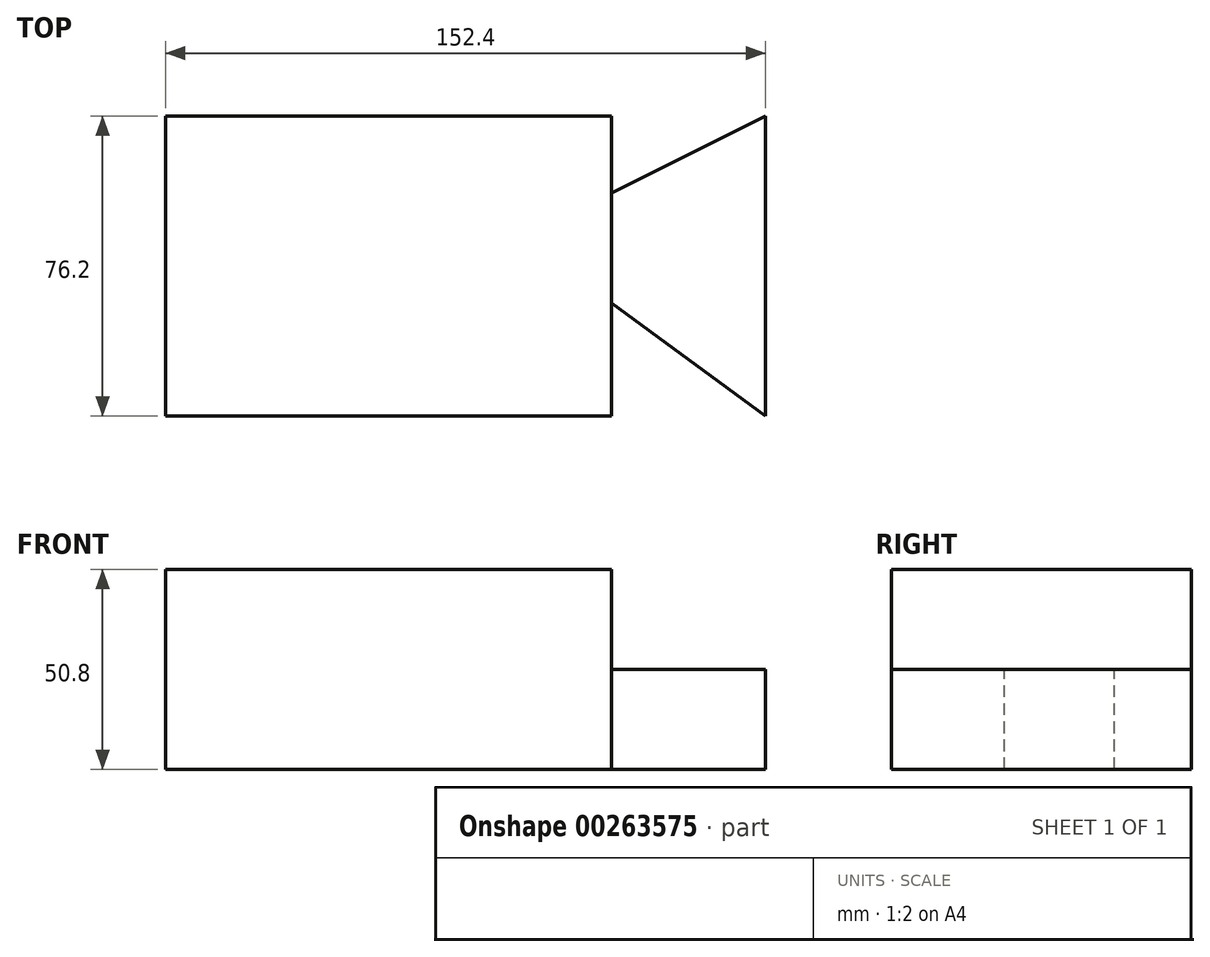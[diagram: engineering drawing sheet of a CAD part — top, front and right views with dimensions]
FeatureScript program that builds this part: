
annotation { "Feature Type Name" : "Feature", "Feature Type Description" : "" }
export const myFeature = defineFeature(function(context is Context, id is Id, definition is map)
    precondition{}
    {
        {
            var Q0;
            Q0=qCreatedBy(makeId("Front.planeOp"),FACE);
            var sketch = newSketch(context, id + "F0", { "sketchPlane" : qUnion([Q0])});
            skLineSegment(sketch, "E0.bottom", {"start": v(-73.83, 13.67) * mm, "end": v(78.57, 13.67) * mm});
            skLineSegment(sketch, "E0.top", {"start": v(-73.83, -37.13) * mm, "end": v(78.57, -37.13) * mm});
            skLineSegment(sketch, "E0.left", {"start": v(-73.83, 13.67) * mm, "end": v(-73.83, -37.13) * mm});
            skLineSegment(sketch, "E0.right", {"start": v(78.57, 13.67) * mm, "end": v(78.57, -37.13) * mm});
            skSolve(sketch);
        }
        {
            var Q0;
            Q0 = qSketchRegion(id + "F0", true);
            extrude(context, id + "F1", {"entities" : qUnion([Q0]), "depth" : 76.2 * mm});
        }
        {
            var Q0;
            Q0=makeQuery(id+"F1.opExtrude","SWEPT_FACE",FACE,{"disambiguationData":[OSD([sQuery(id+"F0.wireOp",EDGE,"E0.bottom")])]});
            var sketch = newSketch(context, id + "F2", { "sketchPlane" : qUnion([Q0])});
            skLineSegment(sketch, "E1", {"start": v(78.57, -76.2) * mm, "end": v(39.48, -47.56) * mm});
            skLineSegment(sketch, "E2", {"start": v(39.48, -19.5) * mm, "end": v(78.57, 0) * mm});
            skLineSegment(sketch, "E3", {"start": v(39.48, -19.5) * mm, "end": v(39.48, 0) * mm});
            skLineSegment(sketch, "E4", {"start": v(39.48, 0) * mm, "end": v(78.57, 0) * mm});
            skLineSegment(sketch, "E5", {"start": v(39.48, -47.56) * mm, "end": v(39.48, -76.2) * mm});
            skLineSegment(sketch, "E6", {"start": v(39.48, -76.2) * mm, "end": v(78.57, -76.2) * mm});
            skSolve(sketch);
        }
        {
            var Q0;
            Q0 = qSketchRegion(id + "F2", true);
            extrude(context, id + "F3", {"entities" : qUnion([Q0]), "operationType" : NewBodyOperationType.REMOVE, "endBound" : BoundingType.THROUGH_ALL, "oppositeDirection" : true, "depth" : 25.4 * mm});
        }
        {
            var Q0;
            Q0=makeQuery(id+"F3.boolean.opBoolean","COPY",FACE,{"derivedFrom":makeQuery(id+"F3.opExtrude","SWEPT_FACE",FACE,{"disambiguationData":[OSD([sQuery(id+"F2.wireOp",EDGE,"E1")])]})});
            var sketch = newSketch(context, id + "F4", { "sketchPlane" : qUnion([Q0])});
            skLineSegment(sketch, "E7", {"start": v(59.95, -11.73) * mm, "end": v(108.42, -11.73) * mm});
            skLineSegment(sketch, "E8", {"start": v(108.42, -11.73) * mm, "end": v(108.42, 13.67) * mm});
            skLineSegment(sketch, "E9", {"start": v(108.42, 13.67) * mm, "end": v(59.95, 13.67) * mm});
            skLineSegment(sketch, "E10", {"start": v(59.95, 13.67) * mm, "end": v(59.95, -11.73) * mm});
            skSolve(sketch);
        }
        {
            var Q0;
            Q0=makeQuery(id+"F4.imprint","IMPRINT",FACE,{"disambiguationData":[TD([[makeQuery(id+"F4.imprint","IMPRINT",EDGE,{"derivedFrom":sQuery(id+"F4.wireOp",EDGE,"E7")}),1.0]])]});
            extrude(context, id + "F5", {"entities" : qUnion([Q0]), "operationType" : NewBodyOperationType.REMOVE, "endBound" : BoundingType.THROUGH_ALL, "oppositeDirection" : true, "depth" : 25.4 * mm});
        }
        {
            var Q0;
            Q0=makeQuery(id+"F5.boolean.opBoolean","COPY",FACE,{"derivedFrom":makeQuery(id+"F5.opExtrude","SWEPT_FACE",FACE,{"disambiguationData":[OSD([sQuery(id+"F4.wireOp",EDGE,"E10")])]})});
            var sketch = newSketch(context, id + "F6", { "sketchPlane" : qUnion([Q0])});
            skLineSegment(sketch, "E11", {"start": v(-15.03, -11.73) * mm, "end": v(-15.03, 13.67) * mm});
            skLineSegment(sketch, "E12", {"start": v(-15.03, 13.67) * mm, "end": v(39.8, 13.67) * mm});
            skLineSegment(sketch, "E13", {"start": v(39.8, 13.67) * mm, "end": v(39.8, -11.73) * mm});
            skLineSegment(sketch, "E14", {"start": v(39.8, -11.73) * mm, "end": v(-15.03, -11.73) * mm});
            skSolve(sketch);
        }
        {
            var Q0;
            Q0=makeQuery(id+"F1.opExtrude","SWEPT_FACE",FACE,{"disambiguationData":[OSD([sQuery(id+"F0.wireOp",EDGE,"E0.bottom")])]});
            var sketch = newSketch(context, id + "F7", { "sketchPlane" : qUnion([Q0])});
            skLineSegment(sketch, "E15", {"start": v(39.48, -47.56) * mm, "end": v(39.48, -19.5) * mm});
            skLineSegment(sketch, "E16", {"start": v(39.48, -19.5) * mm, "end": v(71.88, -3.34) * mm});
            skLineSegment(sketch, "E17", {"start": v(71.88, -3.34) * mm, "end": v(39.48, -47.56) * mm});
            skLineSegment(sketch, "E18", {"start": v(39.48, -47.56) * mm, "end": v(60.04, -83.17) * mm});
            skLineSegment(sketch, "E19", {"start": v(60.04, -83.17) * mm, "end": v(93.5, -40.1) * mm});
            skLineSegment(sketch, "E20", {"start": v(93.5, -40.1) * mm, "end": v(71.88, -3.34) * mm});
            skSolve(sketch);
        }
        {
            var Q0;
            Q0 = qSketchRegion(id + "F7", true);
            extrude(context, id + "F8", {"entities" : qUnion([Q0]), "operationType" : NewBodyOperationType.REMOVE, "oppositeDirection" : true, "depth" : 25.4 * mm});
        }
    });
